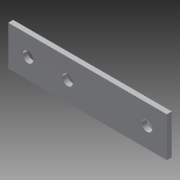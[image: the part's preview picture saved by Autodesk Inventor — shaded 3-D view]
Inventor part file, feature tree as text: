
AUTODESK INVENTOR PART (.ipt)
format: ipt  version: 2013 (Build 170138000, 138)  size: 83,968 bytes
history: native  units: in
note: dims shown in document units (in); Inventor stores cm internally (conversion verified against a paired STEP export)
features: extrude x1, sketch x1
ambient origin geometry x8: Origin, YZ Plane, XZ Plane, XY Plane, X Axis, Y Axis, Z Axis, Center Point
feature tree (2):
  extrude  "Extrusion2"  Depth=4.0in
  sketch  "Sketch1"  dims[d0=1.0in d1=4.0in d2=0.266in d3=0.266in d4=0.875in d5=0.5in d6=0.5in d7=0.5in d10=0.266in d11=1.25in d12=0.125in d13=0.0in d14=0.5in]
